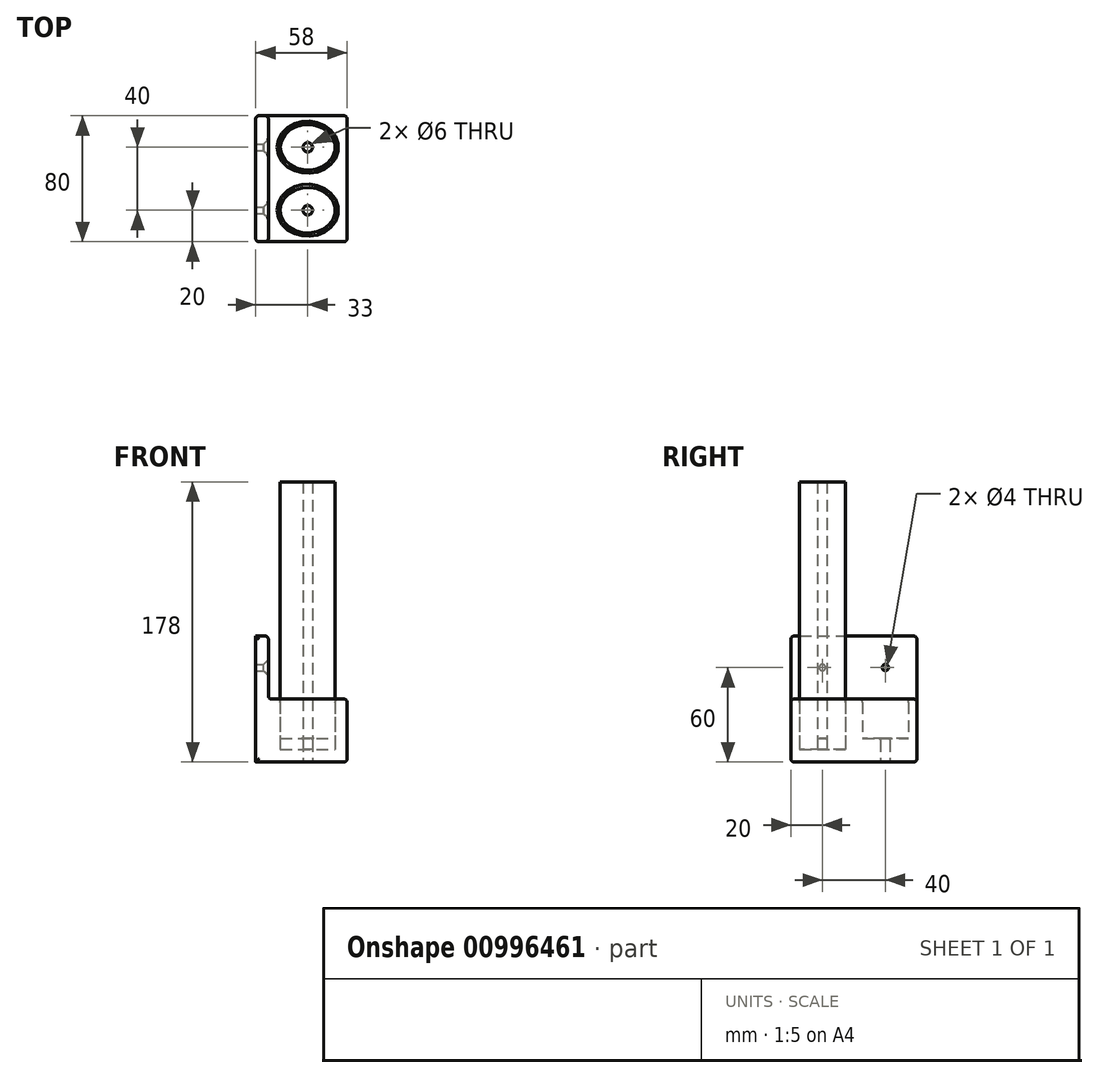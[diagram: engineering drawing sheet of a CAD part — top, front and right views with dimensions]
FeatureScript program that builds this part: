
annotation { "Feature Type Name" : "Feature", "Feature Type Description" : "" }
export const myFeature = defineFeature(function(context is Context, id is Id, definition is map)
    precondition{}
    {
        {
            assignVariable(context, id + "F0", {"name" : "hoehe", "anyValue" : 40});
        }
        {
            var Q0;
            Q0=qCreatedBy(makeId("Top.planeOp"),FACE);
            var sketch = newSketch(context, id + "F1", { "sketchPlane" : qUnion([Q0])});
            skLineSegment(sketch, "E0.bottom", {"start": v(17.5, -14.5) * mm, "end": v(-17.5, -14.5) * mm, "construction": true});
            skLineSegment(sketch, "E0.top", {"start": v(17.5, 14.5) * mm, "end": v(-17.5, 14.5) * mm, "construction": true});
            skLineSegment(sketch, "E0.left", {"start": v(17.5, -14.5) * mm, "end": v(17.5, 14.5) * mm, "construction": true});
            skLineSegment(sketch, "E0.right", {"start": v(-17.5, -14.5) * mm, "end": v(-17.5, 14.5) * mm, "construction": true});
            skPoint(sketch, "E0.middle", {"position": v(0, 0) * mm});
            skEllipse(sketch, "E1", {"center": v(0, 0) * mm, "majorRadius": 17.5 * mm, "minorRadius": 14.5 * mm, "majorAxis": v(-1, 0)});
            skLineSegment(sketch, "E2.bottom", {"start": v(25, -20) * mm, "end": v(-25, -20) * mm});
            skLineSegment(sketch, "E2.top", {"start": v(25, 20) * mm, "end": v(-25, 20) * mm});
            skLineSegment(sketch, "E2.left", {"start": v(25, -20) * mm, "end": v(25, 20) * mm});
            skLineSegment(sketch, "E2.right", {"start": v(-25, -20) * mm, "end": v(-25, 20) * mm});
            skCircle(sketch, "E3", {"center": v(0, 0) * mm, "radius": 3 * mm});
            skLineSegment(sketch, "E4.bottom", {"start": v(-25, 20) * mm, "end": v(-33, 20) * mm});
            skLineSegment(sketch, "E4.top", {"start": v(-25, -20) * mm, "end": v(-33, -20) * mm});
            skLineSegment(sketch, "E4.left", {"start": v(-25, 20) * mm, "end": v(-25, -20) * mm});
            skLineSegment(sketch, "E4.right", {"start": v(-33, 20) * mm, "end": v(-33, -20) * mm});
            skLineSegment(sketch, "E5.MirrorCS", {"start": v(-33, 20) * mm, "end": v(-33, 60) * mm});
            skLineSegment(sketch, "E6.MirrorCS", {"start": v(-25, 20) * mm, "end": v(-25, 60) * mm});
            skLineSegment(sketch, "E7.MirrorCS", {"start": v(-25, 60) * mm, "end": v(-33, 60) * mm});
            skLineSegment(sketch, "E8.MirrorCS", {"start": v(25, 60) * mm, "end": v(-25, 60) * mm});
            skLineSegment(sketch, "E9.MirrorCS", {"start": v(25, 60) * mm, "end": v(25, 20) * mm});
            skEllipse(sketch, "E10.MirrorC", {"center": v(0, 40) * mm, "majorRadius": 17.5 * mm, "minorRadius": 14.5 * mm, "majorAxis": v(-1, 0)});
            skCircle(sketch, "E11.MirrorC", {"center": v(0, 40) * mm, "radius": 3 * mm});
            skSolve(sketch);
        }
        {
            var Q0;
            Q0=makeQuery(id+"F1.imprint","IMPRINT",FACE,{"disambiguationData":[TD([[makeQuery(id+"F1.imprint","IMPRINT",EDGE,{"derivedFrom":sQuery(id+"F1.wireOp",EDGE,"E4.bottom")}),-1.0]])]});
            var Q1;
            Q1=makeQuery(id+"F1.imprint","IMPRINT",FACE,{"disambiguationData":[TD([[makeQuery(id+"F1.imprint","IMPRINT",EDGE,{"derivedFrom":sQuery(id+"F1.wireOp",EDGE,"E4.top")}),-1.0]])]});
            extrude(context, id + "F2", {"entities" : qUnion([Q0, Q1]), "depth" : 2 * getVariable(context, 'hoehe') * mm, "offsetDistance" : 25 * mm});
        }
        {
            var Q0;
            Q0=makeQuery(id+"F1.imprint","IMPRINT",FACE,{"disambiguationData":[TD([[makeQuery(id+"F1.imprint","IMPRINT",EDGE,{"derivedFrom":sQuery(id+"F1.wireOp",EDGE,"E2.top")}),-1.0]])]});
            var Q1;
            Q1=makeQuery(id+"F1.imprint","IMPRINT",FACE,{"disambiguationData":[TD([[makeQuery(id+"F1.imprint","IMPRINT",EDGE,{"derivedFrom":sQuery(id+"F1.wireOp",EDGE,"E1")}),-1.0]])]});
            extrude(context, id + "F3", {"entities" : qUnion([Q0, Q1]), "operationType" : NewBodyOperationType.ADD, "depth" : (getVariable(context, 'hoehe')) * mm, "offsetDistance" : 25 * mm});
        }
        {
            var Q0;
            Q0=makeQuery(id+"F1.imprint","IMPRINT",FACE,{"disambiguationData":[TD([[makeQuery(id+"F1.imprint","IMPRINT",EDGE,{"derivedFrom":sQuery(id+"F1.wireOp",EDGE,"E10.MirrorC")}),1.0]])]});
            var Q1;
            Q1=makeQuery(id+"F1.imprint","IMPRINT",FACE,{"disambiguationData":[TD([[makeQuery(id+"F1.imprint","IMPRINT",EDGE,{"derivedFrom":sQuery(id+"F1.wireOp",EDGE,"E1")}),1.0]])]});
            extrude(context, id + "F4", {"entities" : qUnion([Q0, Q1]), "operationType" : NewBodyOperationType.ADD, "depth" : 8 * mm, "offsetDistance" : 25 * mm});
        }
        {
            var Q0;
            Q0 = qSketchRegion(id + "F1", true);
            var Q1;
            Q1=makeQuery(id+"F1.imprint","IMPRINT",FACE,{"disambiguationData":[TD([[makeQuery(id+"F1.imprint","IMPRINT",EDGE,{"derivedFrom":sQuery(id+"F1.wireOp",EDGE,"E11.MirrorC")}),-1.0]])]});
            var Q2;
            Q2=makeQuery(id+"F1.imprint","IMPRINT",FACE,{"disambiguationData":[TD([[makeQuery(id+"F1.imprint","IMPRINT",EDGE,{"derivedFrom":sQuery(id+"F1.wireOp",EDGE,"E3")}),1.0]])]});
            extrude(context, id + "F5", {"entities" : qUnion([Q0, Q1, Q2]), "operationType" : NewBodyOperationType.ADD, "depth" : 15 * mm, "offsetDistance" : 25 * mm});
        }
        {
            var Q0;
            Q0=makeQuery(id+"F2.opExtrude","SWEPT_FACE",FACE,{"disambiguationData":[OSD([sQuery(id+"F1.wireOp",EDGE,"E4.left"),sQuery(id+"F1.wireOp",EDGE,"E6.MirrorCS")])]});
            var sketch = newSketch(context, id + "F6", { "sketchPlane" : qUnion([Q0])});
            skLineSegment(sketch, "E12", {"start": v(-20, 80) * mm, "end": v(-20, 60) * mm, "construction": true});
            skLineSegment(sketch, "E13", {"start": v(-20, 60) * mm, "end": v(60, 60) * mm, "construction": true});
            skLineSegment(sketch, "E14", {"start": v(60, 60) * mm, "end": v(60, 70) * mm, "construction": true});
            skPoint(sketch, "E14.endSnap0", {"position": v(-20, 70) * mm});
            skLineSegment(sketch, "E15", {"start": v(60, 70) * mm, "end": v(-20, 70) * mm, "construction": true});
            skLineSegment(sketch, "E16", {"start": v(20, 80) * mm, "end": v(20, 40) * mm, "construction": true});
            skPoint(sketch, "E17", {"position": v(96.35, 105.6) * mm});
            skLineSegment(sketch, "E18", {"start": v(0, 40) * mm, "end": v(0, 80) * mm, "construction": true});
            skPoint(sketch, "E19", {"position": v(0, 60) * mm});
            skPoint(sketch, "E20.MirrorP", {"position": v(40, 60) * mm});
            skSolve(sketch);
        }
        {
            var Q0;
            Q0=sQuery(id+"F6.wireOp",VERTEX,"E19");
            var Q1;
            Q1=sQuery(id+"F6.wireOp",VERTEX,"E20.MirrorP");
            var Q2;
            Q2=makeQuery(id+"F2.opExtrude","SWEPT_BODY",BODY,{"disambiguationData":[OSD([sQuery(id+"F1.wireOp",EDGE,"E4.top"),sQuery(id+"F1.wireOp",EDGE,"E4.left"),sQuery(id+"F1.wireOp",EDGE,"E4.right"),sQuery(id+"F1.wireOp",EDGE,"E5.MirrorCS"),sQuery(id+"F1.wireOp",EDGE,"E6.MirrorCS"),sQuery(id+"F1.wireOp",EDGE,"E7.MirrorCS")])]});
            hole(context, id + "F7", {"style" : HoleStyle.C_SINK, "endStyle" : HoleEndStyle.THROUGH, "holeDiameter" : 4 * mm, "cSinkDiameter" : 10 * mm, "cSinkAngle" : 90 * degree, "majorDiameter" : 5 * mm, "isTappedThrough" : true, "tappedDepth" : 12 * mm, "tapClearance" : 3, "locations" : qUnion([Q0, Q1]), "scope" : qUnion([Q2])});
        }
        {
            var Q0;
            Q0=makeQuery(id+"F3.opExtrude","CAP_FACE",FACE,{"disambiguationData":[OSD([sQuery(id+"F1.wireOp",EDGE,"E1"),sQuery(id+"F1.wireOp",EDGE,"E2.bottom"),sQuery(id+"F1.wireOp",EDGE,"E2.left"),sQuery(id+"F1.wireOp",EDGE,"E4.left"),sQuery(id+"F1.wireOp",EDGE,"E6.MirrorCS"),sQuery(id+"F1.wireOp",EDGE,"E8.MirrorCS"),sQuery(id+"F1.wireOp",EDGE,"E9.MirrorCS"),sQuery(id+"F1.wireOp",EDGE,"E10.MirrorC")])],"isStart":false});
            var Q1;
            Q1=makeQuery(id+"F3.boolean.opBoolean","MERGE",FACE,{"derivedFrom":[makeQuery(id+"F2.opExtrude","SWEPT_FACE",FACE,{"disambiguationData":[OSD([sQuery(id+"F1.wireOp",EDGE,"E7.MirrorCS")])]}),makeQuery(id+"F3.opExtrude","SWEPT_FACE",FACE,{"disambiguationData":[OSD([sQuery(id+"F1.wireOp",EDGE,"E8.MirrorCS")])]})]});
            var Q2;
            Q2=makeQuery(id+"F3.opExtrude","SWEPT_FACE",FACE,{"disambiguationData":[OSD([sQuery(id+"F1.wireOp",EDGE,"E2.left"),sQuery(id+"F1.wireOp",EDGE,"E9.MirrorCS")])]});
            var Q3;
            Q3=makeQuery(id+"F3.boolean.opBoolean","MERGE",FACE,{"derivedFrom":[makeQuery(id+"F2.opExtrude","SWEPT_FACE",FACE,{"disambiguationData":[OSD([sQuery(id+"F1.wireOp",EDGE,"E4.top")])]}),makeQuery(id+"F3.opExtrude","SWEPT_FACE",FACE,{"disambiguationData":[OSD([sQuery(id+"F1.wireOp",EDGE,"E2.bottom")])]})]});
            var Q4;
            Q4=makeQuery(id+"F2.opExtrude","SWEPT_FACE",FACE,{"disambiguationData":[OSD([sQuery(id+"F1.wireOp",EDGE,"E4.left"),sQuery(id+"F1.wireOp",EDGE,"E6.MirrorCS")])]});
            fillet(context, id + "F8", {"entities" : qUnion([Q0, Q1, Q2, Q3, Q4]), "radius" : 2 * mm, "tangentPropagation" : true, "allowEdgeOverflow" : false});
        }
        {
            var Q0;
            Q0=makeQuery(id+"F5.opExtrude","CAP_EDGE",EDGE,{"disambiguationData":[OSD([sQuery(id+"F1.wireOp",EDGE,"E3")])],"isStart":false});
            var Q1;
            Q1=makeQuery(id+"F5.opExtrude","CAP_EDGE",EDGE,{"disambiguationData":[OSD([sQuery(id+"F1.wireOp",EDGE,"E11.MirrorC")])],"isStart":false});
            var Q2;
            Q2=makeQuery(id+"F4.opExtrude","CAP_EDGE",EDGE,{"disambiguationData":[OSD([sQuery(id+"F1.wireOp",EDGE,"E3")])],"isStart":false});
            var Q3;
            Q3=makeQuery(id+"F4.opExtrude","CAP_EDGE",EDGE,{"disambiguationData":[OSD([sQuery(id+"F1.wireOp",EDGE,"E11.MirrorC")])],"isStart":false});
            fillet(context, id + "F9", {"entities" : qUnion([Q0, Q1, Q2, Q3]), "radius" : 1 * mm, "tangentPropagation" : true, "allowEdgeOverflow" : false});
        }
        {
            var Q0;
            Q0=makeQuery(id+"F4.opExtrude","CAP_FACE",FACE,{"disambiguationData":[OSD([sQuery(id+"F1.wireOp",EDGE,"E1"),sQuery(id+"F1.wireOp",EDGE,"E3")])],"isStart":false});
            var Q1;
            Q1=makeQuery(id+"F4.opExtrude","CAP_FACE",FACE,{"disambiguationData":[OSD([sQuery(id+"F1.wireOp",EDGE,"E10.MirrorC"),sQuery(id+"F1.wireOp",EDGE,"E11.MirrorC")])],"isStart":false});
            extrude(context, id + "F10", {"entities" : qUnion([Q0, Q1]), "depth" : 170 * mm, "offsetDistance" : 25 * mm});
        }
    });
